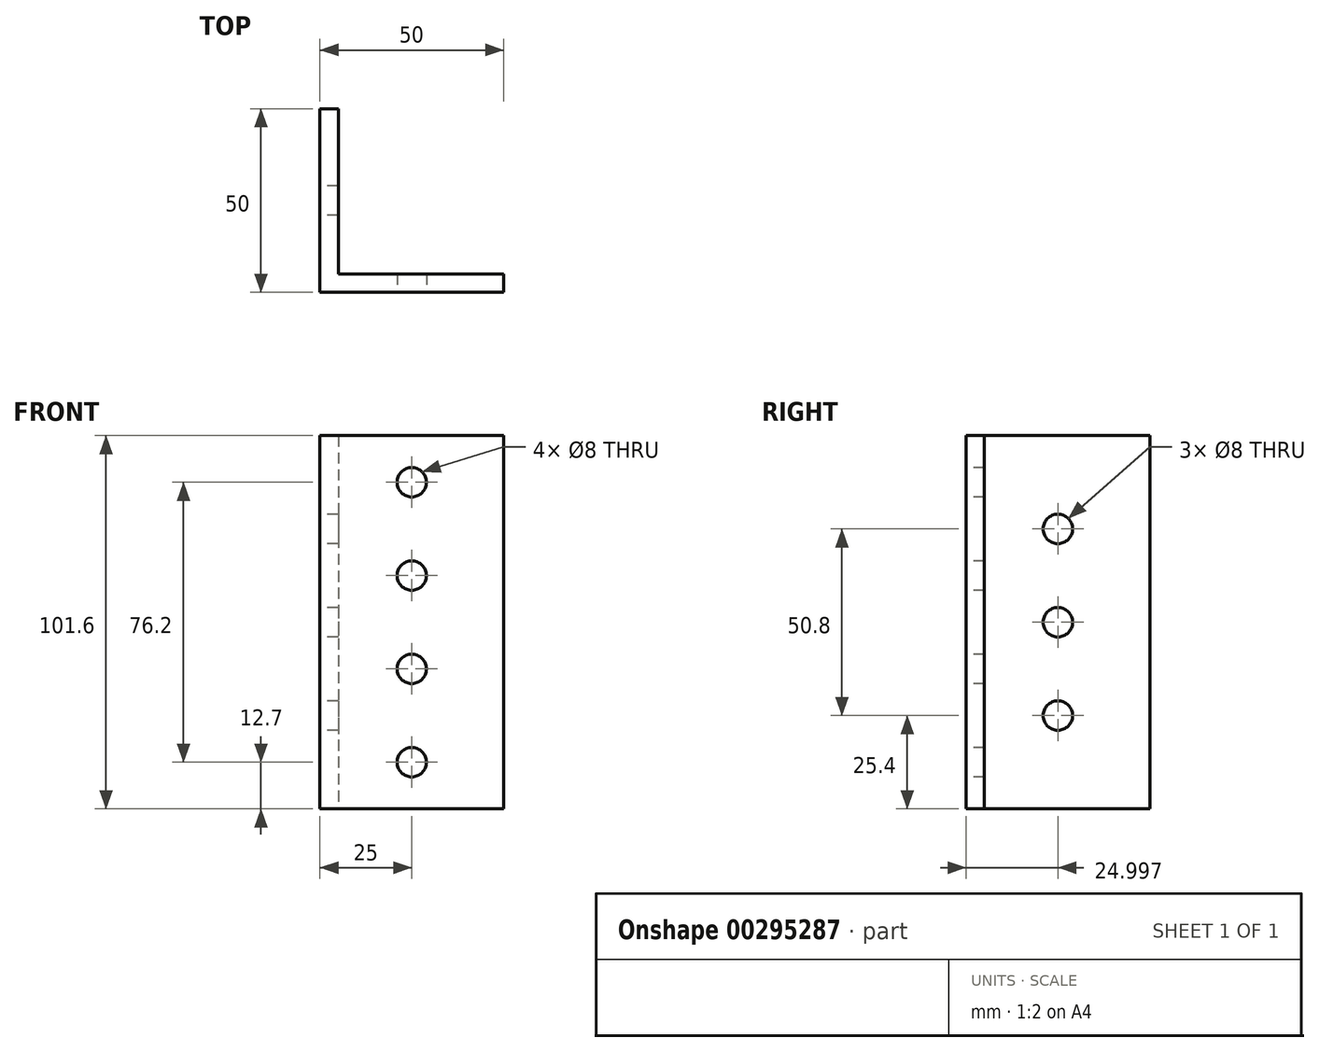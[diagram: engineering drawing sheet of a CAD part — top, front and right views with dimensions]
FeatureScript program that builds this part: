
annotation { "Feature Type Name" : "Feature", "Feature Type Description" : "" }
export const myFeature = defineFeature(function(context is Context, id is Id, definition is map)
    precondition{}
    {
        {
            var Q0;
            Q0=qCreatedBy(makeId("Top.planeOp"),FACE);
            var sketch = newSketch(context, id + "F0", { "sketchPlane" : qUnion([Q0])});
            skLineSegment(sketch, "E0", {"start": v(-50, 12.93) * mm, "end": v(-50, -37.07) * mm});
            skLineSegment(sketch, "E1", {"start": v(-50, -37.07) * mm, "end": v(0, -37.07) * mm});
            skLineSegment(sketch, "E2", {"start": v(0, -37.07) * mm, "end": v(0, -32.07) * mm});
            skLineSegment(sketch, "E3", {"start": v(0, -32.07) * mm, "end": v(-45, -32.07) * mm});
            skLineSegment(sketch, "E4", {"start": v(-45, -32.07) * mm, "end": v(-45, 12.93) * mm});
            skLineSegment(sketch, "E5", {"start": v(-45, 12.93) * mm, "end": v(-50, 12.93) * mm});
            skSolve(sketch);
        }
        {
            var Q0;
            Q0=makeQuery(id+"F0.imprint","IMPRINT",FACE,{"disambiguationData":[TD([[makeQuery(id+"F0.imprint","IMPRINT",EDGE,{"derivedFrom":sQuery(id+"F0.wireOp",EDGE,"E0")}),1.0]])]});
            extrude(context, id + "F1", {"entities" : qUnion([Q0]), "depth" : 101.6 * mm});
        }
        {
            var Q0;
            Q0=makeQuery(id+"F1.opExtrude","SWEPT_FACE",FACE,{"disambiguationData":[OSD([sQuery(id+"F0.wireOp",EDGE,"E0")])]});
            var sketch = newSketch(context, id + "F2", { "sketchPlane" : qUnion([Q0])});
            skCircle(sketch, "E6", {"center": v(12.07, 76.2) * mm, "radius": 4 * mm});
            skCircle(sketch, "E7", {"center": v(12.07, 50.8) * mm, "radius": 4 * mm});
            skCircle(sketch, "E8", {"center": v(12.07, 25.4) * mm, "radius": 4 * mm});
            skSolve(sketch);
        }
        {
            var Q0;
            Q0 = qSketchRegion(id + "F2", true);
            extrude(context, id + "F3", {"entities" : qUnion([Q0]), "operationType" : NewBodyOperationType.REMOVE, "oppositeDirection" : true, "depth" : 25 * mm});
        }
        {
            var Q0;
            Q0=makeQuery(id+"F1.opExtrude","SWEPT_FACE",FACE,{"disambiguationData":[OSD([sQuery(id+"F0.wireOp",EDGE,"E1")])]});
            var sketch = newSketch(context, id + "F4", { "sketchPlane" : qUnion([Q0])});
            skPoint(sketch, "E9", {"position": v(-25, 88.9) * mm});
            skPoint(sketch, "E10", {"position": v(-25, 63.5) * mm});
            skPoint(sketch, "E11", {"position": v(-25, 38.1) * mm});
            skPoint(sketch, "E12", {"position": v(-25, 12.7) * mm});
            skSolve(sketch);
        }
        {
            var Q0;
            Q0=sQuery(id+"F4.wireOp",VERTEX,"E9");
            var Q1;
            Q1=sQuery(id+"F4.wireOp",VERTEX,"E10");
            var Q2;
            Q2=sQuery(id+"F4.wireOp",VERTEX,"E11");
            var Q3;
            Q3=sQuery(id+"F4.wireOp",VERTEX,"E12");
            var Q4;
            Q4=makeQuery(id+"F1.opExtrude","SWEPT_BODY",BODY,{"disambiguationData":[OSD([sQuery(id+"F0.wireOp",EDGE,"E0"),sQuery(id+"F0.wireOp",EDGE,"E1"),sQuery(id+"F0.wireOp",EDGE,"E2"),sQuery(id+"F0.wireOp",EDGE,"E3"),sQuery(id+"F0.wireOp",EDGE,"E4"),sQuery(id+"F0.wireOp",EDGE,"E5")])]});
            hole(context, id + "F5", {"style" : HoleStyle.SIMPLE, "endStyle" : HoleEndStyle.THROUGH, "standardTappedOrClearance" : lookupTablePath({ "standard" : "ISO", "size" : "8", "type" : "Drilled" }), "standardBlindInLast" : lookupTablePath({ "standard" : "ISO", "size" : "8", "type" : "Drilled" }), "holeDiameter" : 8 * mm, "tappedDepth" : 12 * mm, "tapClearance" : 3, "locations" : qUnion([Q0, Q1, Q2, Q3]), "scope" : qUnion([Q4])});
        }
    });
